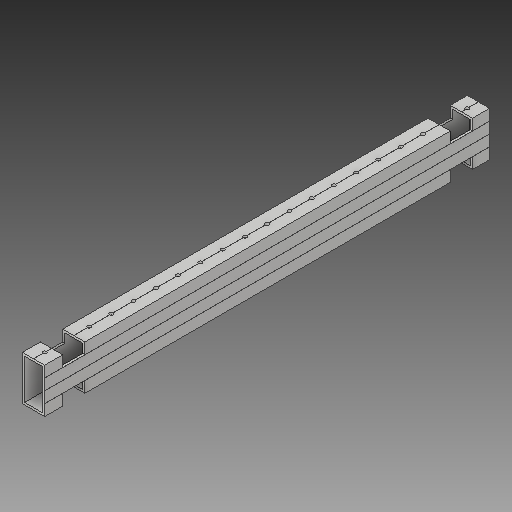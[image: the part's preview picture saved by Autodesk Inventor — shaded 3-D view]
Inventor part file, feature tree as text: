
AUTODESK INVENTOR PART (.ipt)
format: ipt  version: 2017 (Build 210142000, 142)  size: 591,360 bytes
history: native  units: in
note: dims shown in document units (in); Inventor stores cm internally (conversion verified against a paired STEP export)
features: other x6, extrude x3, sketch x3, reference x2
ambient origin geometry x8: Origin, YZ Plane, XZ Plane, XY Plane, X Axis, Y Axis, Z Axis, Center Point
bodies: Solid1 (feature_tree)
feature tree (14):
  extrude  "Extrusion2"  Depth=1.0in TaperAngle=0.0deg
  extrude  "Extrusion3"  Depth=1.0in
  extrude  "Extrusion5"  Depth=0.5in
  sketch  "Sketch1"  dims[d0=20.0in d3=1.0in d4=0.0in]
  sketch  "Sketch2"  dims[d5=1.0in d6=0.0in d7=10.0in]
  reference  "Reference2"
  sketch  "Sketch4"  dims[d15=1.0in d16=0.5in d17=1.0in d18=0.0in]
  reference  "Reference3"
  other  "Cut-Extrude2"
  parser-record x1  (decoder bookkeeping rows leaked as tree rows — omitted from the tree; the rows remain in map.json)
  other  "2898-17-A-0100.iam"
  other  "SideFrame_MIR:1"
  other  "#35_12T_Sprocket_MIR:1"
  other  "2898-17-P-0102:1"
note: 1 file-system path scrubbed to <path> (originals preserved in map.json)
